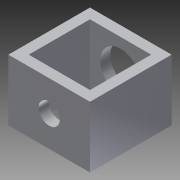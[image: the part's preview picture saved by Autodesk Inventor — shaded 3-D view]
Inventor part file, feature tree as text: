
AUTODESK INVENTOR PART (.ipt)
format: ipt  version: 2014 SP1 (Build 180222100, 222)  size: 103,424 bytes
history: native  units: in
note: dims shown in document units (in); Inventor stores cm internally (conversion verified against a paired STEP export)
features: extrude x3, sketch x3
ambient origin geometry x8: Origin, YZ Plane, XZ Plane, XY Plane, X Axis, Y Axis, Z Axis, Center Point
bodies: Solid1 (feature_tree)
feature tree (6):
  extrude  "Extrusion1"  Depth=1.0in
  extrude  "Extrusion2"  Depth=0.75in TaperAngle=0.0deg
  extrude  "Extrusion3"  Depth=1.0in TaperAngle=0.0deg
  sketch  "Sketch1"  dims[d0=1.0in d1=1.0in]
  sketch  "Sketch2"  dims[d2=0.125in d3=0.75in d4=0.0in]
  sketch  "Sketch3"  dims[d5=0.26in d7=1.0in d8=0.0in d9=0.5in d11=0.125in d12=0.0in]
